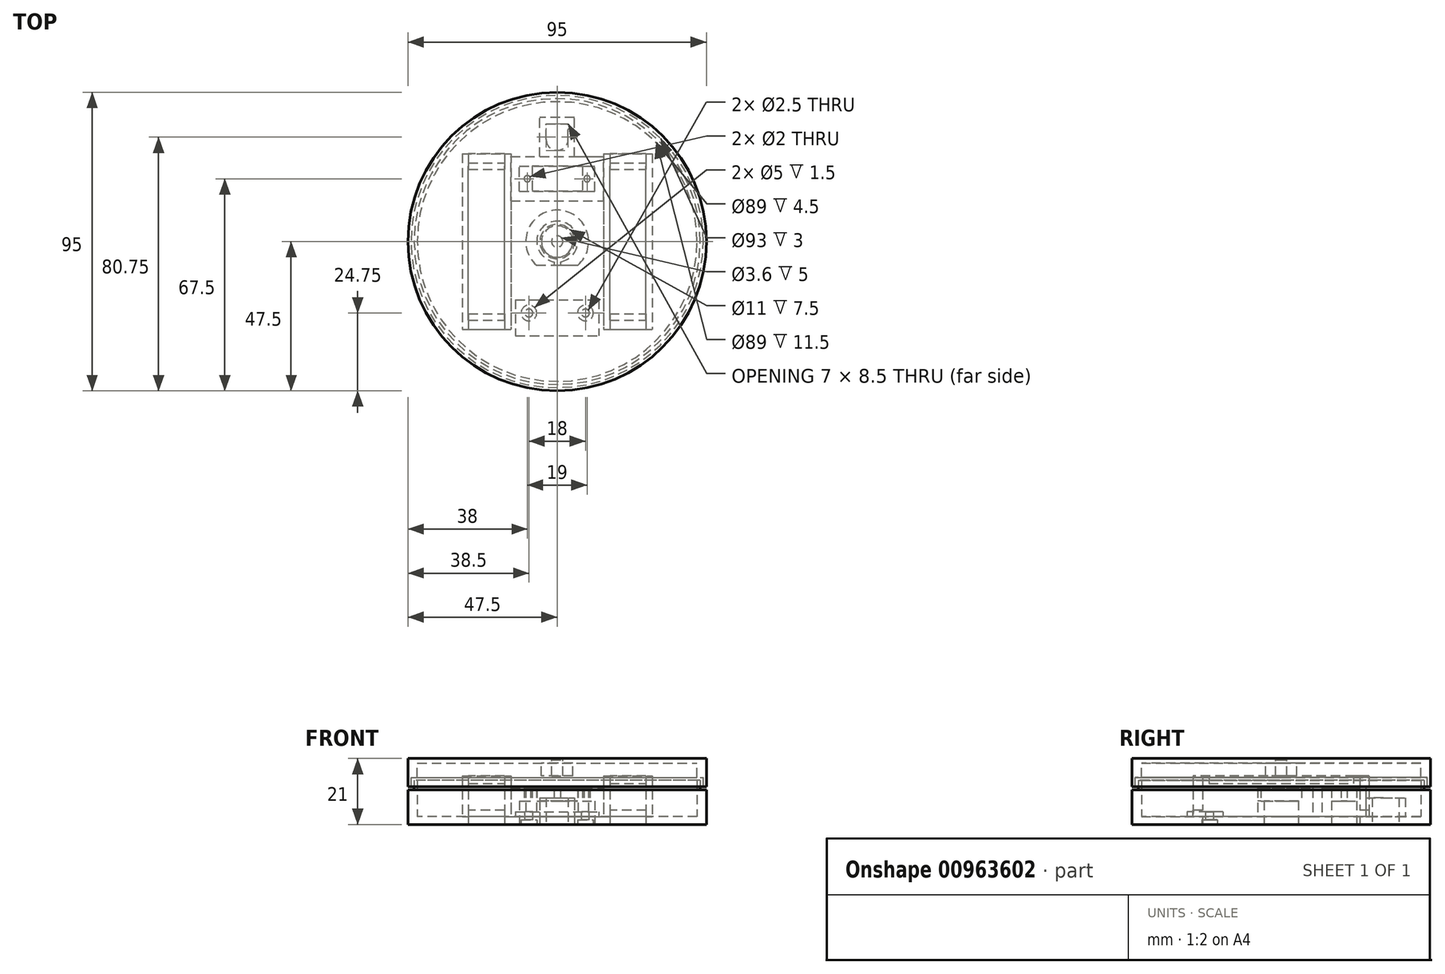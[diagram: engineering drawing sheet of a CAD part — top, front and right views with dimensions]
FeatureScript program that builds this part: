
annotation { "Feature Type Name" : "Feature", "Feature Type Description" : "" }
export const myFeature = defineFeature(function(context is Context, id is Id, definition is map)
    precondition{}
    {
        {
            var Q0;
            Q0=qCreatedBy(makeId("Top.planeOp"),FACE);
            var sketch = newSketch(context, id + "F0", { "sketchPlane" : qUnion([Q0])});
            skCircle(sketch, "E0", {"center": v(0, 0) * mm, "radius": 5.5 * mm});
            skCircle(sketch, "E1", {"center": v(0, 0) * mm, "radius": 47.5 * mm});
            skCircle(sketch, "E2", {"center": v(0, 0) * mm, "radius": 15 * mm, "construction": true});
            skSolve(sketch);
        }
        {
            var Q0;
            Q0=makeQuery(id+"F0.imprint","IMPRINT",FACE,{"disambiguationData":[TD([[makeQuery(id+"F0.imprint","IMPRINT",EDGE,{"derivedFrom":sQuery(id+"F0.wireOp",EDGE,"E0")}),-1.0]])]});
            extrude(context, id + "F1", {"entities" : qUnion([Q0]), "depth" : 2.5 * mm, "offsetDistance" : 25 * mm});
        }
        {
            var Q0;
            Q0=makeQuery(id+"F1.opExtrude","CAP_FACE",FACE,{"disambiguationData":[OSD([sQuery(id+"F0.wireOp",EDGE,"E0"),sQuery(id+"F0.wireOp",EDGE,"E1")])],"isStart":false});
            var sketch = newSketch(context, id + "F2", { "sketchPlane" : qUnion([Q0])});
            skLineSegment(sketch, "E3.bottom", {"start": v(-13.3, -18.5) * mm, "end": v(13.3, -18.5) * mm});
            skLineSegment(sketch, "E3.top", {"start": v(-13.3, -30) * mm, "end": v(13.3, -30) * mm});
            skLineSegment(sketch, "E3.left", {"start": v(-13.3, -18.5) * mm, "end": v(-13.3, -30) * mm});
            skLineSegment(sketch, "E3.right", {"start": v(13.3, -18.5) * mm, "end": v(13.3, -30) * mm});
            skLineSegment(sketch, "E4", {"start": v(0, 0) * mm, "end": v(0, -18.5) * mm, "construction": true});
            skSolve(sketch);
        }
        {
            var Q0;
            Q0=makeQuery(id+"F2.imprint","IMPRINT",FACE,{"disambiguationData":[TD([[makeQuery(id+"F2.imprint","IMPRINT",EDGE,{"derivedFrom":sQuery(id+"F2.wireOp",EDGE,"E3.bottom")}),-1.0]])]});
            extrude(context, id + "F3", {"entities" : qUnion([Q0]), "operationType" : NewBodyOperationType.ADD, "depth" : 1.5 * mm, "offsetDistance" : 25 * mm});
        }
        {
            var Q0;
            Q0=makeQuery(id+"F3.opExtrude","CAP_FACE",FACE,{"disambiguationData":[OSD([sQuery(id+"F2.wireOp",EDGE,"E3.bottom"),sQuery(id+"F2.wireOp",EDGE,"E3.top"),sQuery(id+"F2.wireOp",EDGE,"E3.left"),sQuery(id+"F2.wireOp",EDGE,"E3.right")])],"isStart":false});
            var sketch = newSketch(context, id + "F4", { "sketchPlane" : qUnion([Q0])});
            skCircle(sketch, "E5", {"center": v(-9, -22.75) * mm, "radius": 1.25 * mm});
            skLineSegment(sketch, "E6", {"start": v(-9, -22.75) * mm, "end": v(9, -22.75) * mm, "construction": true});
            skCircle(sketch, "E7", {"center": v(9, -22.75) * mm, "radius": 1.25 * mm});
            skLineSegment(sketch, "E8", {"start": v(0, -18.5) * mm, "end": v(0, -22.75) * mm, "construction": true});
            skSolve(sketch);
        }
        {
            var Q0;
            Q0 = qSketchRegion(id + "F4", true);
            extrude(context, id + "F5", {"entities" : qUnion([Q0]), "operationType" : NewBodyOperationType.REMOVE, "endBound" : BoundingType.THROUGH_ALL, "oppositeDirection" : true, "depth" : 25 * mm, "offsetDistance" : 25 * mm});
        }
        {
            var Q0;
            Q0=makeQuery(id+"F1.opExtrude","CAP_FACE",FACE,{"disambiguationData":[OSD([sQuery(id+"F0.wireOp",EDGE,"E0"),sQuery(id+"F0.wireOp",EDGE,"E1")])],"isStart":false});
            var sketch = newSketch(context, id + "F6", { "sketchPlane" : qUnion([Q0])});
            skArc(sketch, "E9", {"start": v(6.61, -7.5) * mm, "mid": v(0, 10) * mm, "end": v(-6.61, -7.5) * mm});
            skCircle(sketch, "E10", {"center": v(0, 0) * mm, "radius": 5.5 * mm});
            skLineSegment(sketch, "E11", {"start": v(-6.61, -7.5) * mm, "end": v(6.61, -7.5) * mm});
            skSolve(sketch);
        }
        {
            var Q0;
            Q0 = qSketchRegion(id + "F6", true);
            extrude(context, id + "F7", {"entities" : qUnion([Q0]), "operationType" : NewBodyOperationType.ADD, "depth" : 5 * mm, "offsetDistance" : 25 * mm});
        }
        {
            var Q0;
            Q0=makeQuery(id+"F7.opExtrude","CAP_FACE",FACE,{"disambiguationData":[OSD([sQuery(id+"F6.wireOp",EDGE,"E9"),sQuery(id+"F6.wireOp",EDGE,"E10"),sQuery(id+"F6.wireOp",EDGE,"E11")])],"isStart":false});
            var sketch = newSketch(context, id + "F8", { "sketchPlane" : qUnion([Q0])});
            skArc(sketch, "E12.0", {"start": v(6.61, -7.5) * mm, "mid": v(0, 10) * mm, "end": v(-6.61, -7.5) * mm});
            skLineSegment(sketch, "E12.1", {"start": v(-6.61, -7.5) * mm, "end": v(-1, -7.5) * mm});
            skArc(sketch, "E13", {"start": v(1, -6.42) * mm, "mid": v(0, 6.5) * mm, "end": v(-1, -6.42) * mm});
            skLineSegment(sketch, "E14", {"start": v(-1, -6.42) * mm, "end": v(-1, -7.5) * mm});
            skLineSegment(sketch, "E15", {"start": v(1, -6.42) * mm, "end": v(1, -7.5) * mm});
            skLineSegment(sketch, "E16.trimOffspring", {"start": v(1, -7.5) * mm, "end": v(6.61, -7.5) * mm});
            skSolve(sketch);
        }
        {
            var Q0;
            Q0=makeQuery(id+"F8.imprint","IMPRINT",FACE,{"disambiguationData":[TD([[makeQuery(id+"F8.imprint","IMPRINT",EDGE,{"derivedFrom":sQuery(id+"F8.wireOp",EDGE,"E12.0")}),1.0]])]});
            extrude(context, id + "F9", {"entities" : qUnion([Q0]), "operationType" : NewBodyOperationType.ADD, "depth" : 4 * mm, "offsetDistance" : 25 * mm});
        }
        {
            var Q0;
            Q0=makeQuery(id+"F1.opExtrude","CAP_FACE",FACE,{"disambiguationData":[OSD([sQuery(id+"F0.wireOp",EDGE,"E0"),sQuery(id+"F0.wireOp",EDGE,"E1")])],"isStart":true});
            var sketch = newSketch(context, id + "F10", { "sketchPlane" : qUnion([Q0])});
            skLineSegment(sketch, "E17.bottom", {"start": v(-12, -16) * mm, "end": v(12, -16) * mm});
            skLineSegment(sketch, "E17.top", {"start": v(-12, -24) * mm, "end": v(12, -24) * mm});
            skLineSegment(sketch, "E17.left", {"start": v(-12, -16) * mm, "end": v(-12, -24) * mm});
            skLineSegment(sketch, "E17.right", {"start": v(12, -16) * mm, "end": v(12, -24) * mm});
            skSolve(sketch);
        }
        {
            var Q0;
            Q0=makeQuery(id+"F1.opExtrude","CAP_FACE",FACE,{"disambiguationData":[OSD([sQuery(id+"F0.wireOp",EDGE,"E0"),sQuery(id+"F0.wireOp",EDGE,"E1")])],"isStart":false});
            var sketch = newSketch(context, id + "F11", { "sketchPlane" : qUnion([Q0])});
            skLineSegment(sketch, "E18.bottom", {"start": v(-15, 27) * mm, "end": v(15, 27) * mm});
            skLineSegment(sketch, "E18.top", {"start": v(-15, 13) * mm, "end": v(15, 13) * mm});
            skLineSegment(sketch, "E18.left", {"start": v(-15, 27) * mm, "end": v(-15, 13) * mm});
            skLineSegment(sketch, "E18.right", {"start": v(15, 27) * mm, "end": v(15, 13) * mm});
            skSolve(sketch);
        }
        {
            var Q0;
            Q0=makeQuery(id+"F11.imprint","IMPRINT",FACE,{"disambiguationData":[TD([[makeQuery(id+"F11.imprint","IMPRINT",EDGE,{"derivedFrom":sQuery(id+"F11.wireOp",EDGE,"E18.bottom")}),-1.0]])]});
            extrude(context, id + "F12", {"entities" : qUnion([Q0]), "operationType" : NewBodyOperationType.ADD, "depth" : 9 * mm, "offsetDistance" : 25 * mm});
        }
        {
            var Q0;
            Q0=makeQuery(id+"F10.imprint","IMPRINT",FACE,{"disambiguationData":[TD([[makeQuery(id+"F10.imprint","IMPRINT",EDGE,{"derivedFrom":sQuery(id+"F10.wireOp",EDGE,"E17.bottom")}),-1.0]])]});
            extrude(context, id + "F13", {"entities" : qUnion([Q0]), "operationType" : NewBodyOperationType.REMOVE, "oppositeDirection" : true, "depth" : 7.5 * mm, "offsetDistance" : 25 * mm});
        }
        {
            var Q0;
            Q0=makeQuery(id+"F13.boolean.opBoolean","COPY",FACE,{"derivedFrom":makeQuery(id+"F13.opExtrude","CAP_FACE",FACE,{"disambiguationData":[OSD([sQuery(id+"F10.wireOp",EDGE,"E17.bottom"),sQuery(id+"F10.wireOp",EDGE,"E17.top"),sQuery(id+"F10.wireOp",EDGE,"E17.left"),sQuery(id+"F10.wireOp",EDGE,"E17.right")])],"isStart":false})});
            var sketch = newSketch(context, id + "F14", { "sketchPlane" : qUnion([Q0])});
            skLineSegment(sketch, "E19.bottom", {"start": v(-8, -16) * mm, "end": v(8, -16) * mm});
            skLineSegment(sketch, "E19.top", {"start": v(-8, -24) * mm, "end": v(8, -24) * mm});
            skLineSegment(sketch, "E19.left", {"start": v(-8, -16) * mm, "end": v(-8, -24) * mm});
            skLineSegment(sketch, "E19.right", {"start": v(8, -16) * mm, "end": v(8, -24) * mm});
            skLineSegment(sketch, "E20", {"start": v(-8, -20) * mm, "end": v(-9.5, -20) * mm, "construction": true});
            skCircle(sketch, "E21", {"center": v(-9.5, -20) * mm, "radius": 1 * mm});
            skCircle(sketch, "E22", {"center": v(9.5, -20) * mm, "radius": 1 * mm});
            skSolve(sketch);
        }
        {
            var Q0;
            Q0=makeQuery(id+"F14.imprint","IMPRINT",FACE,{"disambiguationData":[TD([[makeQuery(id+"F14.imprint","IMPRINT",EDGE,{"derivedFrom":sQuery(id+"F14.wireOp",EDGE,"E19.bottom")}),-1.0]])]});
            var Q1;
            Q1=makeQuery(id+"F14.imprint","IMPRINT",FACE,{"disambiguationData":[TD([[makeQuery(id+"F14.imprint","IMPRINT",EDGE,{"derivedFrom":sQuery(id+"F14.wireOp",EDGE,"E21")}),1.0]])]});
            var Q2;
            Q2=makeQuery(id+"F14.imprint","IMPRINT",FACE,{"disambiguationData":[TD([[makeQuery(id+"F14.imprint","IMPRINT",EDGE,{"derivedFrom":sQuery(id+"F14.wireOp",EDGE,"E22")}),1.0]])]});
            extrude(context, id + "F15", {"entities" : qUnion([Q0, Q1, Q2]), "operationType" : NewBodyOperationType.REMOVE, "endBound" : BoundingType.THROUGH_ALL, "oppositeDirection" : true, "depth" : 25 * mm, "offsetDistance" : 25 * mm});
        }
        {
            var Q0;
            Q0=makeQuery(id+"F1.opExtrude","CAP_FACE",FACE,{"disambiguationData":[OSD([sQuery(id+"F0.wireOp",EDGE,"E0"),sQuery(id+"F0.wireOp",EDGE,"E1")])],"isStart":true});
            var sketch = newSketch(context, id + "F16", { "sketchPlane" : qUnion([Q0])});
            skLineSegment(sketch, "E23.bottom", {"start": v(-28.25, 25) * mm, "end": v(-16.75, 25) * mm});
            skLineSegment(sketch, "E23.top", {"start": v(-28.25, -25) * mm, "end": v(-16.75, -25) * mm});
            skLineSegment(sketch, "E23.left", {"start": v(-28.25, 25) * mm, "end": v(-28.25, -25) * mm});
            skLineSegment(sketch, "E23.right", {"start": v(-16.75, 25) * mm, "end": v(-16.75, -25) * mm});
            skLineSegment(sketch, "E24.bottom", {"start": v(16.75, 25) * mm, "end": v(28.25, 25) * mm});
            skLineSegment(sketch, "E24.top", {"start": v(16.75, -25) * mm, "end": v(28.25, -25) * mm});
            skLineSegment(sketch, "E24.left", {"start": v(16.75, 25) * mm, "end": v(16.75, -25) * mm});
            skLineSegment(sketch, "E24.right", {"start": v(28.25, 25) * mm, "end": v(28.25, -25) * mm});
            skPoint(sketch, "E25", {"position": v(-22.5, -25) * mm});
            skPoint(sketch, "E26", {"position": v(22.5, -25) * mm});
            skSolve(sketch);
        }
        {
            var Q0;
            Q0=makeQuery(id+"F1.opExtrude","CAP_FACE",FACE,{"disambiguationData":[OSD([sQuery(id+"F0.wireOp",EDGE,"E0"),sQuery(id+"F0.wireOp",EDGE,"E1")])],"isStart":false});
            var sketch = newSketch(context, id + "F17", { "sketchPlane" : qUnion([Q0])});
            skLineSegment(sketch, "E27.bottom", {"start": v(-30.25, 28) * mm, "end": v(-14.75, 28) * mm});
            skLineSegment(sketch, "E27.top", {"start": v(-30.25, -28) * mm, "end": v(-14.75, -28) * mm});
            skLineSegment(sketch, "E27.left", {"start": v(-30.25, 28) * mm, "end": v(-30.25, -28) * mm});
            skLineSegment(sketch, "E27.right", {"start": v(-14.75, 28) * mm, "end": v(-14.75, -28) * mm});
            skLineSegment(sketch, "E28.bottom", {"start": v(14.75, 28) * mm, "end": v(30.25, 28) * mm});
            skLineSegment(sketch, "E28.top", {"start": v(14.75, -28) * mm, "end": v(30.25, -28) * mm});
            skLineSegment(sketch, "E28.left", {"start": v(14.75, 28) * mm, "end": v(14.75, -28) * mm});
            skLineSegment(sketch, "E28.right", {"start": v(30.25, 28) * mm, "end": v(30.25, -28) * mm});
            skPoint(sketch, "E29", {"position": v(-22.5, -28) * mm});
            skPoint(sketch, "E30", {"position": v(22.5, -28) * mm});
            skCircle(sketch, "E31", {"center": v(0, 0) * mm, "radius": 15 * mm, "construction": true});
            skSolve(sketch);
        }
        {
            var Q0;
            Q0 = qSketchRegion(id + "F17", true);
            extrude(context, id + "F18", {"entities" : qUnion([Q0]), "operationType" : NewBodyOperationType.ADD, "depth" : 13 * mm, "offsetDistance" : 25 * mm});
        }
        {
            var Q0;
            Q0=makeQuery(id+"F16.imprint","IMPRINT",FACE,{"disambiguationData":[TD([[makeQuery(id+"F16.imprint","IMPRINT",EDGE,{"derivedFrom":sQuery(id+"F16.wireOp",EDGE,"E23.bottom")}),-1.0]])]});
            var Q1;
            Q1=makeQuery(id+"F16.imprint","IMPRINT",FACE,{"disambiguationData":[TD([[makeQuery(id+"F16.imprint","IMPRINT",EDGE,{"derivedFrom":sQuery(id+"F16.wireOp",EDGE,"E24.bottom")}),-1.0]])]});
            extrude(context, id + "F19", {"entities" : qUnion([Q0, Q1]), "operationType" : NewBodyOperationType.REMOVE, "oppositeDirection" : true, "depth" : 13 * mm, "offsetDistance" : 25 * mm});
        }
        {
            var Q0;
            Q0=makeQuery(id+"F19.boolean.opBoolean","COPY",FACE,{"derivedFrom":makeQuery(id+"F19.opExtrude","CAP_FACE",FACE,{"disambiguationData":[OSD([sQuery(id+"F16.wireOp",EDGE,"E24.bottom"),sQuery(id+"F16.wireOp",EDGE,"E24.top"),sQuery(id+"F16.wireOp",EDGE,"E24.left"),sQuery(id+"F16.wireOp",EDGE,"E24.right")])],"isStart":false})});
            var sketch = newSketch(context, id + "F20", { "sketchPlane" : qUnion([Q0])});
            skLineSegment(sketch, "E32.bottom", {"start": v(16.75, 25) * mm, "end": v(28.25, 25) * mm});
            skLineSegment(sketch, "E32.top", {"start": v(16.75, 23) * mm, "end": v(28.25, 23) * mm});
            skLineSegment(sketch, "E32.left", {"start": v(16.75, 25) * mm, "end": v(16.75, 23) * mm});
            skLineSegment(sketch, "E32.right", {"start": v(28.25, 25) * mm, "end": v(28.25, 23) * mm});
            skLineSegment(sketch, "E33.bottom", {"start": v(16.75, -25) * mm, "end": v(28.25, -25) * mm});
            skLineSegment(sketch, "E33.top", {"start": v(16.75, -23) * mm, "end": v(28.25, -23) * mm});
            skLineSegment(sketch, "E33.left", {"start": v(16.75, -25) * mm, "end": v(16.75, -23) * mm});
            skLineSegment(sketch, "E33.right", {"start": v(28.25, -25) * mm, "end": v(28.25, -23) * mm});
            skSolve(sketch);
        }
        {
            var Q0;
            Q0=makeQuery(id+"F19.boolean.opBoolean","COPY",FACE,{"derivedFrom":makeQuery(id+"F19.opExtrude","CAP_FACE",FACE,{"disambiguationData":[OSD([sQuery(id+"F16.wireOp",EDGE,"E23.bottom"),sQuery(id+"F16.wireOp",EDGE,"E23.top"),sQuery(id+"F16.wireOp",EDGE,"E23.left"),sQuery(id+"F16.wireOp",EDGE,"E23.right")])],"isStart":false})});
            var sketch = newSketch(context, id + "F21", { "sketchPlane" : qUnion([Q0])});
            skLineSegment(sketch, "E34.bottom", {"start": v(-28.25, 25) * mm, "end": v(-16.75, 25) * mm});
            skLineSegment(sketch, "E34.top", {"start": v(-28.25, 23) * mm, "end": v(-16.75, 23) * mm});
            skLineSegment(sketch, "E34.left", {"start": v(-28.25, 25) * mm, "end": v(-28.25, 23) * mm});
            skLineSegment(sketch, "E34.right", {"start": v(-16.75, 25) * mm, "end": v(-16.75, 23) * mm});
            skLineSegment(sketch, "E35.bottom", {"start": v(-28.25, -25) * mm, "end": v(-16.75, -25) * mm});
            skLineSegment(sketch, "E35.top", {"start": v(-28.25, -23) * mm, "end": v(-16.75, -23) * mm});
            skLineSegment(sketch, "E35.left", {"start": v(-28.25, -25) * mm, "end": v(-28.25, -23) * mm});
            skLineSegment(sketch, "E35.right", {"start": v(-16.75, -25) * mm, "end": v(-16.75, -23) * mm});
            skSolve(sketch);
        }
        {
            var Q0;
            Q0=makeQuery(id+"F21.imprint","IMPRINT",FACE,{"disambiguationData":[TD([[makeQuery(id+"F21.imprint","IMPRINT",EDGE,{"derivedFrom":sQuery(id+"F21.wireOp",EDGE,"E34.bottom")}),-1.0]])]});
            var Q1;
            Q1=makeQuery(id+"F21.imprint","IMPRINT",FACE,{"disambiguationData":[TD([[makeQuery(id+"F21.imprint","IMPRINT",EDGE,{"derivedFrom":sQuery(id+"F21.wireOp",EDGE,"E35.bottom")}),1.0]])]});
            var Q2;
            Q2=makeQuery(id+"F20.imprint","IMPRINT",FACE,{"disambiguationData":[TD([[makeQuery(id+"F20.imprint","IMPRINT",EDGE,{"derivedFrom":sQuery(id+"F20.wireOp",EDGE,"E33.bottom")}),1.0]])]});
            var Q3;
            Q3=makeQuery(id+"F20.imprint","IMPRINT",FACE,{"disambiguationData":[TD([[makeQuery(id+"F20.imprint","IMPRINT",EDGE,{"derivedFrom":sQuery(id+"F20.wireOp",EDGE,"E32.bottom")}),-1.0]])]});
            extrude(context, id + "F22", {"entities" : qUnion([Q0, Q1, Q2, Q3]), "operationType" : NewBodyOperationType.REMOVE, "endBound" : BoundingType.THROUGH_ALL, "oppositeDirection" : true, "depth" : 25 * mm, "offsetDistance" : 25 * mm});
        }
        {
            var Q0;
            Q0=makeQuery(id+"F18.opExtrude","SWEPT_FACE",FACE,{"disambiguationData":[OSD([sQuery(id+"F17.wireOp",EDGE,"E28.top")])]});
            var sketch = newSketch(context, id + "F23", { "sketchPlane" : qUnion([Q0])});
            skLineSegment(sketch, "E36.bottom", {"start": v(16.75, 2.5) * mm, "end": v(28.25, 2.5) * mm});
            skLineSegment(sketch, "E36.top", {"start": v(16.75, 4.5) * mm, "end": v(28.25, 4.5) * mm});
            skLineSegment(sketch, "E36.left", {"start": v(16.75, 2.5) * mm, "end": v(16.75, 4.5) * mm});
            skLineSegment(sketch, "E36.right", {"start": v(28.25, 2.5) * mm, "end": v(28.25, 4.5) * mm});
            skSolve(sketch);
        }
        {
            var Q0;
            Q0=makeQuery(id+"F23.imprint","IMPRINT",FACE,{"disambiguationData":[TD([[makeQuery(id+"F23.imprint","IMPRINT",EDGE,{"derivedFrom":sQuery(id+"F23.wireOp",EDGE,"E36.bottom")}),1.0]])]});
            extrude(context, id + "F24", {"entities" : qUnion([Q0]), "operationType" : NewBodyOperationType.REMOVE, "endBound" : BoundingType.THROUGH_ALL, "oppositeDirection" : true, "depth" : 25 * mm, "offsetDistance" : 25 * mm});
        }
        {
            var Q0;
            Q0=makeQuery(id+"F18.opExtrude","SWEPT_FACE",FACE,{"disambiguationData":[OSD([sQuery(id+"F17.wireOp",EDGE,"E27.top")])]});
            var sketch = newSketch(context, id + "F25", { "sketchPlane" : qUnion([Q0])});
            skLineSegment(sketch, "E37.bottom", {"start": v(-28.25, 2.5) * mm, "end": v(-16.75, 2.5) * mm});
            skLineSegment(sketch, "E37.top", {"start": v(-28.25, 4.5) * mm, "end": v(-16.75, 4.5) * mm});
            skLineSegment(sketch, "E37.left", {"start": v(-28.25, 2.5) * mm, "end": v(-28.25, 4.5) * mm});
            skLineSegment(sketch, "E37.right", {"start": v(-16.75, 2.5) * mm, "end": v(-16.75, 4.5) * mm});
            skSolve(sketch);
        }
        {
            var Q0;
            Q0=makeQuery(id+"F25.imprint","IMPRINT",FACE,{"disambiguationData":[TD([[makeQuery(id+"F25.imprint","IMPRINT",EDGE,{"derivedFrom":sQuery(id+"F25.wireOp",EDGE,"E37.bottom")}),1.0]])]});
            extrude(context, id + "F26", {"entities" : qUnion([Q0]), "operationType" : NewBodyOperationType.REMOVE, "endBound" : BoundingType.THROUGH_ALL, "oppositeDirection" : true, "depth" : 25 * mm, "offsetDistance" : 25 * mm});
        }
        {
            var Q0;
            Q0=makeQuery(id+"F26.boolean.opBoolean","MERGE",FACE,{"derivedFrom":[makeQuery(id+"F24.boolean.opBoolean","MERGE",FACE,{"derivedFrom":[makeQuery(id+"F1.opExtrude","CAP_FACE",FACE,{"disambiguationData":[OSD([sQuery(id+"F0.wireOp",EDGE,"E0"),sQuery(id+"F0.wireOp",EDGE,"E1")])],"isStart":false})],"fromTools":[makeQuery(id+"F24.opExtrude","SWEPT_FACE",FACE,{"disambiguationData":[OSD([sQuery(id+"F23.wireOp",EDGE,"E36.bottom")])]})]})],"fromTools":[makeQuery(id+"F26.opExtrude","SWEPT_FACE",FACE,{"disambiguationData":[OSD([sQuery(id+"F25.wireOp",EDGE,"E37.bottom")])]})]});
            var sketch = newSketch(context, id + "F27", { "sketchPlane" : qUnion([Q0])});
            skLineSegment(sketch, "E38.top", {"start": v(-3.5, 37.5) * mm, "end": v(3.5, 37.5) * mm});
            skLineSegment(sketch, "E38.left", {"start": v(-3.5, 32.5) * mm, "end": v(-3.5, 37.5) * mm});
            skLineSegment(sketch, "E38.right", {"start": v(3.5, 32.5) * mm, "end": v(3.5, 37.5) * mm});
            skArc(sketch, "E39", {"start": v(-3.5, 32.5) * mm, "mid": v(0, 29) * mm, "end": v(3.5, 32.5) * mm});
            skLineSegment(sketch, "E40.bottom", {"start": v(5.5, 27) * mm, "end": v(-5.5, 27) * mm});
            skLineSegment(sketch, "E40.top", {"start": v(5.5, 39.5) * mm, "end": v(-5.5, 39.5) * mm});
            skLineSegment(sketch, "E40.left", {"start": v(5.5, 27) * mm, "end": v(5.5, 39.5) * mm});
            skLineSegment(sketch, "E40.right", {"start": v(-5.5, 27) * mm, "end": v(-5.5, 39.5) * mm});
            skSolve(sketch);
        }
        {
            var Q0;
            Q0=makeQuery(id+"F27.imprint","IMPRINT",FACE,{"disambiguationData":[TD([[makeQuery(id+"F27.imprint","IMPRINT",EDGE,{"derivedFrom":sQuery(id+"F27.wireOp",EDGE,"E38.top")}),1.0]])]});
            extrude(context, id + "F28", {"entities" : qUnion([Q0]), "operationType" : NewBodyOperationType.ADD, "depth" : 6 * mm, "offsetDistance" : 25 * mm});
        }
        {
            var Q0;
            Q0=makeQuery(id+"F28.boolean.opBoolean","SPLIT",FACE,{"disambiguationData":[TD([makeQuery(id+"F28.opExtrude","SWEPT_FACE",FACE,{"disambiguationData":[OSD([sQuery(id+"F27.wireOp",EDGE,"E38.top")])]})])],"derivedFrom":makeQuery(id+"F26.boolean.opBoolean","MERGE",FACE,{"derivedFrom":[makeQuery(id+"F24.boolean.opBoolean","MERGE",FACE,{"derivedFrom":[makeQuery(id+"F1.opExtrude","CAP_FACE",FACE,{"disambiguationData":[OSD([sQuery(id+"F0.wireOp",EDGE,"E0"),sQuery(id+"F0.wireOp",EDGE,"E1")])],"isStart":false})],"fromTools":[makeQuery(id+"F24.opExtrude","SWEPT_FACE",FACE,{"disambiguationData":[OSD([sQuery(id+"F23.wireOp",EDGE,"E36.bottom")])]})]})],"fromTools":[makeQuery(id+"F26.opExtrude","SWEPT_FACE",FACE,{"disambiguationData":[OSD([sQuery(id+"F25.wireOp",EDGE,"E37.bottom")])]})]})});
            extrude(context, id + "F29", {"entities" : qUnion([Q0]), "operationType" : NewBodyOperationType.REMOVE, "endBound" : BoundingType.THROUGH_ALL, "oppositeDirection" : true, "depth" : 25 * mm, "offsetDistance" : 25 * mm});
        }
        {
            var Q0;
            {var subQ0=sQuery(id+"F0.wireOp",EDGE,"E1");Q0=makeQuery(id+"F28.boolean.opBoolean","SPLIT",FACE,{"disambiguationData":[TD([makeQuery(id+"F1.opExtrude","SWEPT_FACE",FACE,{"disambiguationData":[OSD([subQ0])]})])],"derivedFrom":makeQuery(id+"F26.boolean.opBoolean","MERGE",FACE,{"derivedFrom":[makeQuery(id+"F24.boolean.opBoolean","MERGE",FACE,{"derivedFrom":[makeQuery(id+"F1.opExtrude","CAP_FACE",FACE,{"disambiguationData":[OSD([sQuery(id+"F0.wireOp",EDGE,"E0"),subQ0])],"isStart":false})],"fromTools":[makeQuery(id+"F24.opExtrude","SWEPT_FACE",FACE,{"disambiguationData":[OSD([sQuery(id+"F23.wireOp",EDGE,"E36.bottom")])]})]})],"fromTools":[makeQuery(id+"F26.opExtrude","SWEPT_FACE",FACE,{"disambiguationData":[OSD([sQuery(id+"F25.wireOp",EDGE,"E37.bottom")])]})]})});}
            var sketch = newSketch(context, id + "F30", { "sketchPlane" : qUnion([Q0])});
            skCircle(sketch, "E41.0", {"center": v(0, 0) * mm, "radius": 47.5 * mm});
            skCircle(sketch, "E42", {"center": v(0, 0) * mm, "radius": 44.5 * mm});
            skSolve(sketch);
        }
        {
            var Q0;
            Q0=makeQuery(id+"F30.imprint","IMPRINT",FACE,{"disambiguationData":[TD([[makeQuery(id+"F30.imprint","IMPRINT",EDGE,{"derivedFrom":sQuery(id+"F30.wireOp",EDGE,"E41.0")}),1.0]])]});
            extrude(context, id + "F31", {"entities" : qUnion([Q0]), "operationType" : NewBodyOperationType.ADD, "depth" : 8.5 * mm, "offsetDistance" : 25 * mm});
        }
        {
            var Q0;
            Q0=makeQuery(id+"F31.opExtrude","CAP_FACE",FACE,{"disambiguationData":[OSD([sQuery(id+"F30.wireOp",EDGE,"E41.0"),sQuery(id+"F30.wireOp",EDGE,"E42")])],"isStart":false});
            var sketch = newSketch(context, id + "F32", { "sketchPlane" : qUnion([Q0])});
            skCircle(sketch, "E43.0", {"center": v(0, 0) * mm, "radius": 44.5 * mm});
            skCircle(sketch, "E44", {"center": v(0, 0) * mm, "radius": 45.5 * mm});
            skSolve(sketch);
        }
        {
            var Q0;
            Q0=makeQuery(id+"F32.imprint","IMPRINT",FACE,{"disambiguationData":[TD([[makeQuery(id+"F32.imprint","IMPRINT",EDGE,{"derivedFrom":sQuery(id+"F32.wireOp",EDGE,"E43.0")}),-1.0]])]});
            extrude(context, id + "F33", {"entities" : qUnion([Q0]), "operationType" : NewBodyOperationType.ADD, "depth" : 3 * mm, "offsetDistance" : 25 * mm});
        }
        {
            var Q0;
            Q0=makeQuery(id+"F1.opExtrude","CAP_FACE",FACE,{"disambiguationData":[OSD([sQuery(id+"F0.wireOp",EDGE,"E0"),sQuery(id+"F0.wireOp",EDGE,"E1")])],"isStart":true});
            var sketch = newSketch(context, id + "F34", { "sketchPlane" : qUnion([Q0])});
            skCircle(sketch, "E45.0", {"center": v(9, 22.75) * mm, "radius": 1.25 * mm});
            skCircle(sketch, "E45.1", {"center": v(-9, 22.75) * mm, "radius": 1.25 * mm});
            skCircle(sketch, "E46", {"center": v(-9, 22.75) * mm, "radius": 2.5 * mm});
            skCircle(sketch, "E47", {"center": v(9, 22.75) * mm, "radius": 2.5 * mm});
            skSolve(sketch);
        }
        {
            var Q0;
            Q0=makeQuery(id+"F34.imprint","IMPRINT",FACE,{"disambiguationData":[TD([[makeQuery(id+"F34.imprint","IMPRINT",EDGE,{"derivedFrom":sQuery(id+"F34.wireOp",EDGE,"E45.1")}),1.0]])]});
            var Q1;
            Q1=makeQuery(id+"F34.imprint","IMPRINT",FACE,{"disambiguationData":[TD([[makeQuery(id+"F34.imprint","IMPRINT",EDGE,{"derivedFrom":sQuery(id+"F34.wireOp",EDGE,"E45.0")}),1.0]])]});
            extrude(context, id + "F35", {"entities" : qUnion([Q0, Q1]), "operationType" : NewBodyOperationType.REMOVE, "oppositeDirection" : true, "depth" : 1.5 * mm, "offsetDistance" : 25 * mm});
        }
        {
            var Q0;
            Q0=qCreatedBy(makeId("Top.planeOp"),FACE);
            cPlane(context, id + "F36", {"entities" : qUnion([Q0]), "cplaneType" : CPlaneType.OFFSET, "offset" : 21 * mm, "width" : 150 * mm, "height" : 150 * mm});
        }
        {
            var Q0;
            Q0=qCreatedBy(id+"F36.planeOp",FACE);
            var sketch = newSketch(context, id + "F37", { "sketchPlane" : qUnion([Q0])});
            skCircle(sketch, "E48", {"center": v(0, 0) * mm, "radius": 47.5 * mm});
            skSolve(sketch);
        }
        {
            var Q0;
            Q0=makeQuery(id+"F37.imprint","IMPRINT",FACE,{"disambiguationData":[TD([[makeQuery(id+"F37.imprint","IMPRINT",EDGE,{"derivedFrom":sQuery(id+"F37.wireOp",EDGE,"E48")}),1.0]])]});
            extrude(context, id + "F38", {"entities" : qUnion([Q0]), "oppositeDirection" : true, "depth" : 1.5 * mm, "offsetDistance" : 25 * mm});
        }
        {
            var Q0;
            Q0=makeQuery(id+"F38.opExtrude","CAP_FACE",FACE,{"disambiguationData":[OSD([sQuery(id+"F37.wireOp",EDGE,"E48")])],"isStart":false});
            var sketch = newSketch(context, id + "F39", { "sketchPlane" : qUnion([Q0])});
            skCircle(sketch, "E49", {"center": v(0, 0) * mm, "radius": 44.5 * mm});
            skCircle(sketch, "E50.0", {"center": v(0, 0) * mm, "radius": 47.5 * mm});
            skSolve(sketch);
        }
        {
            var Q0;
            Q0=makeQuery(id+"F39.imprint","IMPRINT",FACE,{"disambiguationData":[TD([[makeQuery(id+"F39.imprint","IMPRINT",EDGE,{"derivedFrom":sQuery(id+"F39.wireOp",EDGE,"E49")}),-1.0]])]});
            extrude(context, id + "F40", {"entities" : qUnion([Q0]), "operationType" : NewBodyOperationType.ADD, "depth" : 4.5 * mm, "offsetDistance" : 25 * mm});
        }
        {
            var Q0;
            Q0=makeQuery(id+"F40.opExtrude","CAP_FACE",FACE,{"disambiguationData":[OSD([sQuery(id+"F39.wireOp",EDGE,"E49"),sQuery(id+"F39.wireOp",EDGE,"E50.0")])],"isStart":false});
            var sketch = newSketch(context, id + "F41", { "sketchPlane" : qUnion([Q0])});
            skCircle(sketch, "E51.0", {"center": v(0, 0) * mm, "radius": 47.5 * mm});
            skCircle(sketch, "E52", {"center": v(0, 0) * mm, "radius": 46.5 * mm});
            skSolve(sketch);
        }
        {
            var Q0;
            Q0 = qSketchRegion(id + "F41", true);
            extrude(context, id + "F42", {"entities" : qUnion([Q0]), "operationType" : NewBodyOperationType.ADD, "depth" : 3 * mm, "offsetDistance" : 25 * mm});
        }
        {
            var Q0;
            Q0=makeQuery(id+"F38.opExtrude","CAP_FACE",FACE,{"disambiguationData":[OSD([sQuery(id+"F37.wireOp",EDGE,"E48")])],"isStart":false});
            var sketch = newSketch(context, id + "F43", { "sketchPlane" : qUnion([Q0])});
            skCircle(sketch, "E53", {"center": v(0, 0) * mm, "radius": 1.8 * mm});
            skCircle(sketch, "E54", {"center": v(0, 0) * mm, "radius": 5 * mm});
            skSolve(sketch);
        }
        {
            var Q0;
            Q0=makeQuery(id+"F43.imprint","IMPRINT",FACE,{"disambiguationData":[TD([[makeQuery(id+"F43.imprint","IMPRINT",EDGE,{"derivedFrom":sQuery(id+"F43.wireOp",EDGE,"E53")}),-1.0]])]});
            extrude(context, id + "F44", {"entities" : qUnion([Q0]), "operationType" : NewBodyOperationType.ADD, "depth" : 4 * mm, "offsetDistance" : 25 * mm});
        }
        {
            var Q0;
            Q0=makeQuery(id+"F44.boolean.opBoolean","SPLIT",FACE,{"disambiguationData":[TD([makeQuery(id+"F44.opExtrude","SWEPT_FACE",FACE,{"disambiguationData":[OSD([sQuery(id+"F43.wireOp",EDGE,"E53")])]})])],"derivedFrom":makeQuery(id+"F38.opExtrude","CAP_FACE",FACE,{"disambiguationData":[OSD([sQuery(id+"F37.wireOp",EDGE,"E48")])],"isStart":false})});
            extrude(context, id + "F45", {"entities" : qUnion([Q0]), "operationType" : NewBodyOperationType.REMOVE, "oppositeDirection" : true, "depth" : 1 * mm, "offsetDistance" : 25 * mm});
        }
    });
